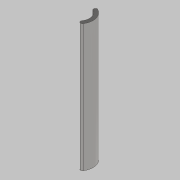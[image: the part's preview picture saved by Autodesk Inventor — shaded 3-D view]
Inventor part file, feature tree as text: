
AUTODESK INVENTOR PART (.ipt)
format: ipt  version: 2021 (Build 250183000, 183)  size: 148,992 bytes
history: native  units: mm
features: fillet x4, extrude x3, sketch x3, sweep x2, projected_geometry x2, other x2, hole x1
ambient origin geometry x8: Origin, YZ Plane, XZ Plane, XY Plane, X Axis, Y Axis, Z Axis, Center Point
bodies: Solid1 (feature_tree)
feature tree (17):
  extrude  "holderProfile"  Depth=3.665191mm
  fillet  "Fillet1"  Radius=2.0mm
  extrude  "holderBase1"  Depth=2.0mm
  fillet  "Fillet2"  Radius=1.0mm
  fillet  "Fillet3"  Radius=70.0mm
  hole  "throughHole"  [1 undecoded]
  sweep  "Sweep1"
  extrude  "Extrusion3"  Depth=1.0mm
  fillet  "Fillet4"  Radius=5.5mm
  sketch  "Sketch1"  dims[d3=12.042772mm d4=3.665191mm d5=2.0mm]
  sketch  "Sketch2"  dims[d6=5.5mm d7=2.0mm d8=1.0mm d9=70.0mm d10=0.0mm]
  projected_geometry  "Projected Loop1"
  other  "throughholePosition"
  sweep  "sweepLine"
  other  "loopProfile"
  sketch  "Sketch7"  dims[d11=1.0mm d12=10.0mm d13=4.0mm d14=0.0mm d15=1.0mm d16=5.5mm d17=3.0mm d18=6.0mm d19=4.0mm d20=2.0mm d21=90.0deg d22=8.0mm d23=0.0mm d26=4.0mm d27=2.0mm d28=0.0mm d29=0.0mm d30=1.75mm d31=0.0mm d32=5.0mm d33=1.0mm]
  projected_geometry  "Projected Loop2"
note: 1 required parameter value undecoded (feature->parameter linkage not recoverable at this tier; creation-order binding heuristic only, values carry confidence <= 0.55)
